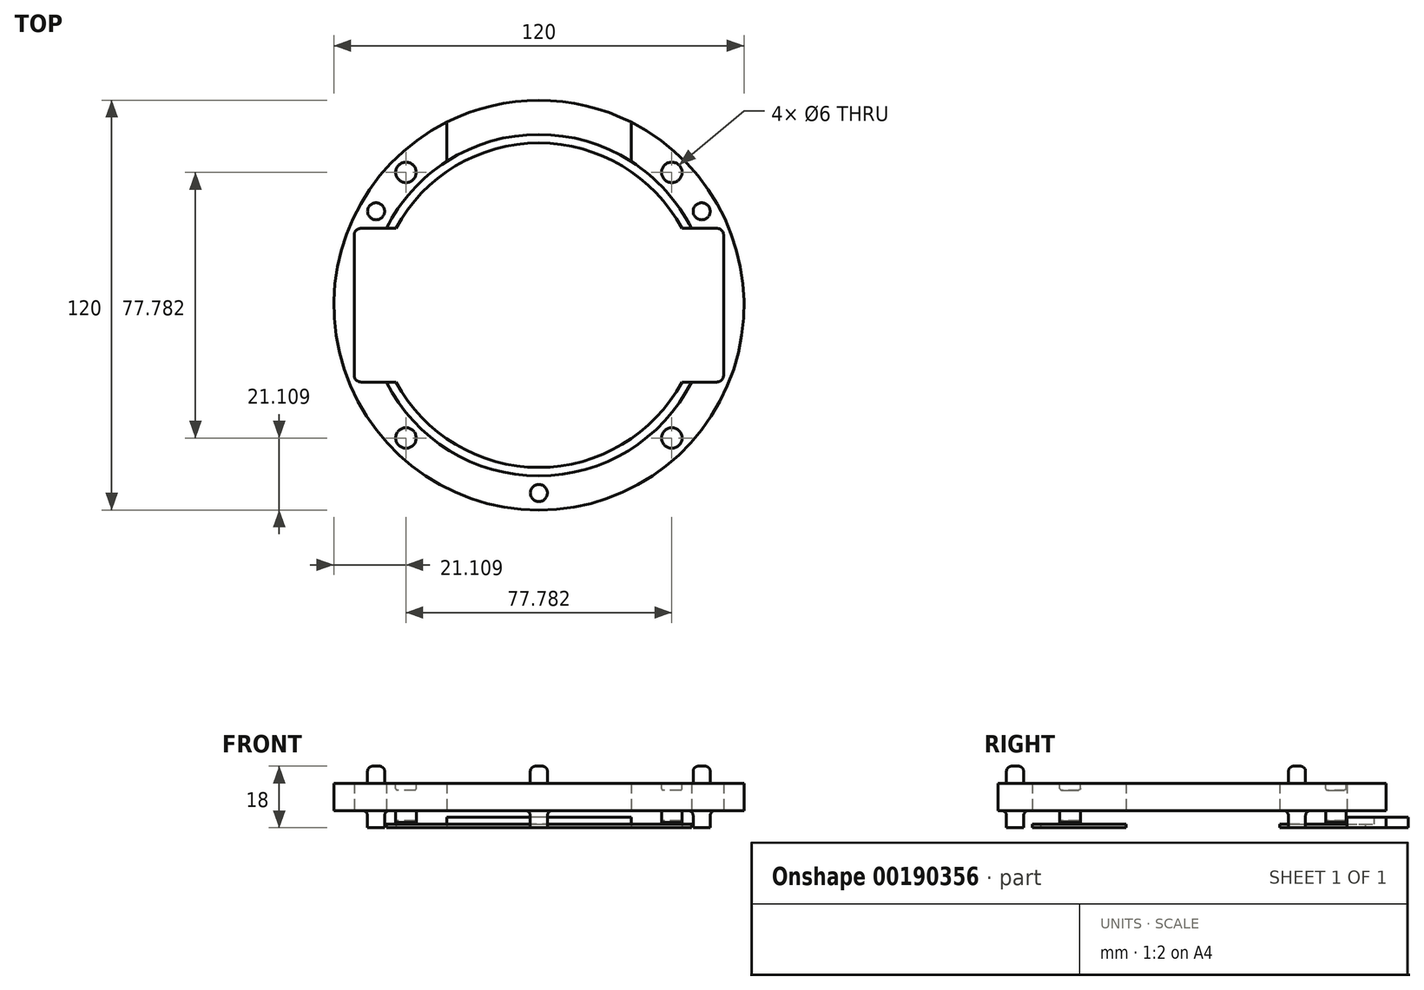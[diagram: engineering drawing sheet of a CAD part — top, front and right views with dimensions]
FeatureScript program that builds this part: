
annotation { "Feature Type Name" : "Feature", "Feature Type Description" : "" }
export const myFeature = defineFeature(function(context is Context, id is Id, definition is map)
    precondition{}
    {
        {
            var Q0;
            Q0=qCreatedBy(makeId("Top.planeOp"),FACE);
            var sketch = newSketch(context, id + "F0", { "sketchPlane" : qUnion([Q0])});
            skCircle(sketch, "E0", {"center": v(0, 0) * mm, "radius": 60 * mm});
            skLineSegment(sketch, "E1", {"start": v(0, 50) * mm, "end": v(0, 50) * mm});
            skArc(sketch, "E2", {"start": v(-44.65, -22.5) * mm, "mid": v(0, -50) * mm, "end": v(44.65, -22.5) * mm});
            skArc(sketch, "E3", {"start": v(-41.83, -22.5) * mm, "mid": v(0, -47.5) * mm, "end": v(41.83, -22.5) * mm});
            skPoint(sketch, "E4.orphan", {"position": v(55.62, -22.5) * mm});
            skLineSegment(sketch, "E5", {"start": v(-44.65, 22.5) * mm, "end": v(-41.83, 22.5) * mm});
            skLineSegment(sketch, "E6", {"start": v(44.65, 22.5) * mm, "end": v(41.83, 22.5) * mm});
            skLineSegment(sketch, "E7.MirrorCS", {"start": v(-44.65, -22.5) * mm, "end": v(-41.83, -22.5) * mm});
            skLineSegment(sketch, "E8.MirrorCS", {"start": v(44.65, -22.5) * mm, "end": v(41.83, -22.5) * mm});
            skArc(sketch, "E9.trimOffspring", {"start": v(41.83, 22.5) * mm, "mid": v(0, 47.5) * mm, "end": v(-41.83, 22.5) * mm});
            skArc(sketch, "E10.trimOffspring", {"start": v(44.65, 22.5) * mm, "mid": v(0, 50) * mm, "end": v(-44.65, 22.5) * mm});
            skLineSegment(sketch, "E11", {"start": v(-27, 53.58) * mm, "end": v(-27, 42.08) * mm});
            skLineSegment(sketch, "E12", {"start": v(27, 53.58) * mm, "end": v(27, 42.08) * mm});
            skLineSegment(sketch, "E13", {"start": v(-27, 53.58) * mm, "end": v(27, 53.58) * mm, "construction": true});
            skLineSegment(sketch, "E14", {"start": v(-44.65, 22.5) * mm, "end": v(-54.05, 22.5) * mm});
            skLineSegment(sketch, "E15", {"start": v(-54.05, 22.5) * mm, "end": v(-54.05, -22.5) * mm});
            skLineSegment(sketch, "E16", {"start": v(-54.05, -22.5) * mm, "end": v(-44.65, -22.5) * mm});
            skLineSegment(sketch, "E17", {"start": v(0, 60) * mm, "end": v(0, -60) * mm, "construction": true});
            skPoint(sketch, "E17.startSnap0", {"position": v(0, 53.58) * mm});
            skPoint(sketch, "E17.endSnap0", {"position": v(0, 47.5) * mm});
            skLineSegment(sketch, "E18.MirrorCS", {"start": v(54.05, 22.5) * mm, "end": v(54.05, -22.5) * mm});
            skLineSegment(sketch, "E19.MirrorCS", {"start": v(44.65, 22.5) * mm, "end": v(54.05, 22.5) * mm});
            skLineSegment(sketch, "E20.MirrorCS", {"start": v(54.05, -22.5) * mm, "end": v(44.65, -22.5) * mm});
            skSolve(sketch);
        }
        {
            var Q0;
            Q0=makeQuery(id+"F0.imprint","IMPRINT",FACE,{"disambiguationData":[TD([[makeQuery(id+"F0.imprint","IMPRINT",EDGE,{"derivedFrom":sQuery(id+"F0.wireOp",EDGE,"E2")}),-1.0]])]});
            extrude(context, id + "F1", {"entities" : qUnion([Q0]), "depth" : 13 * mm});
        }
        {
            var Q0;
            Q0=makeQuery(id+"F1.opExtrude","CAP_FACE",FACE,{"disambiguationData":[OSD([sQuery(id+"F0.wireOp",EDGE,"E0"),sQuery(id+"F0.wireOp",EDGE,"E1")])],"isStart":false});
            var sketch = newSketch(context, id + "F2", { "sketchPlane" : qUnion([Q0])});
            skPoint(sketch, "E21.middle", {"position": v(0, 0) * mm});
            skCircle(sketch, "E22", {"center": v(-38.9, 38.9) * mm, "radius": 3 * mm});
            skCircle(sketch, "E23", {"center": v(-38.9, -38.9) * mm, "radius": 3 * mm});
            skCircle(sketch, "E24", {"center": v(38.9, -38.9) * mm, "radius": 3 * mm});
            skCircle(sketch, "E25", {"center": v(38.9, 38.9) * mm, "radius": 3 * mm});
            skCircle(sketch, "E26", {"center": v(0, -55) * mm, "radius": 2.5 * mm});
            skCircle(sketch, "E27.1.0", {"center": v(47.63, 27.5) * mm, "radius": 2.5 * mm});
            skCircle(sketch, "E27.2.0", {"center": v(-47.63, 27.5) * mm, "radius": 2.5 * mm});
            skSolve(sketch);
        }
        {
            var Q0;
            Q0=makeQuery(id+"F2.imprint","IMPRINT",FACE,{"disambiguationData":[TD([[makeQuery(id+"F2.imprint","IMPRINT",EDGE,{"derivedFrom":sQuery(id+"F2.wireOp",EDGE,"E22")}),1.0]])]});
            var Q1;
            Q1=makeQuery(id+"F2.imprint","IMPRINT",FACE,{"disambiguationData":[TD([[makeQuery(id+"F2.imprint","IMPRINT",EDGE,{"derivedFrom":sQuery(id+"F2.wireOp",EDGE,"E25")}),1.0]])]});
            var Q2;
            Q2=makeQuery(id+"F2.imprint","IMPRINT",FACE,{"disambiguationData":[TD([[makeQuery(id+"F2.imprint","IMPRINT",EDGE,{"derivedFrom":sQuery(id+"F2.wireOp",EDGE,"E24")}),1.0]])]});
            var Q3;
            Q3=makeQuery(id+"F2.imprint","IMPRINT",FACE,{"disambiguationData":[TD([[makeQuery(id+"F2.imprint","IMPRINT",EDGE,{"derivedFrom":sQuery(id+"F2.wireOp",EDGE,"E23")}),1.0]])]});
            extrude(context, id + "F3", {"entities" : qUnion([Q0, Q1, Q2, Q3]), "operationType" : NewBodyOperationType.REMOVE, "oppositeDirection" : true, "depth" : 2 * mm});
        }
        {
            var Q0;
            Q0=makeQuery(id+"F2.imprint","IMPRINT",FACE,{"disambiguationData":[TD([[makeQuery(id+"F2.imprint","IMPRINT",EDGE,{"derivedFrom":sQuery(id+"F2.wireOp",EDGE,"E26")}),1.0]])]});
            var Q1;
            Q1=makeQuery(id+"F2.imprint","IMPRINT",FACE,{"disambiguationData":[TD([[makeQuery(id+"F2.imprint","IMPRINT",EDGE,{"derivedFrom":sQuery(id+"F2.wireOp",EDGE,"E27.1.0")}),1.0]])]});
            var Q2;
            Q2=makeQuery(id+"F2.imprint","IMPRINT",FACE,{"disambiguationData":[TD([[makeQuery(id+"F2.imprint","IMPRINT",EDGE,{"derivedFrom":sQuery(id+"F2.wireOp",EDGE,"E27.2.0")}),1.0]])]});
            var Q3;
            Q3=sQuery(id+"F2.wireOp",EDGE,"VWXdR3C8-mcWa-IJBR-1boV-t68bjsxYqndP");
            var Q4;
            Q4=sQuery(id+"F2.wireOp",EDGE,"uHltdg73-JYHf-iSAY-R7Fn-2nbyHwWvfhgZ");
            var Q5;
            Q5=sQuery(id+"F2.wireOp",EDGE,"R24LEf0a-MQ1t-eLEK-fKfR-x5qMptQUL0lt");
            extrude(context, id + "F4", {"entities" : qUnion([Q0, Q1, Q2]), "operationType" : NewBodyOperationType.ADD, "surfaceEntities" : qUnion([Q3, Q4, Q5]), "depth" : 5 * mm});
        }
        {
            var Q0;
            Q0=makeQuery(id+"F3.boolean.opBoolean","COPY",EDGE,{"derivedFrom":makeQuery(id+"F3.opExtrude","CAP_EDGE",EDGE,{"disambiguationData":[OSD([sQuery(id+"F2.wireOp",EDGE,"E24")])],"isStart":false})});
            var Q1;
            Q1=makeQuery(id+"F3.boolean.opBoolean","COPY",EDGE,{"derivedFrom":makeQuery(id+"F3.opExtrude","CAP_EDGE",EDGE,{"disambiguationData":[OSD([sQuery(id+"F2.wireOp",EDGE,"E23")])],"isStart":false})});
            var Q2;
            Q2=makeQuery(id+"F3.boolean.opBoolean","COPY",EDGE,{"derivedFrom":makeQuery(id+"F3.opExtrude","CAP_EDGE",EDGE,{"disambiguationData":[OSD([sQuery(id+"F2.wireOp",EDGE,"E22")])],"isStart":false})});
            var Q3;
            Q3=makeQuery(id+"F3.boolean.opBoolean","COPY",EDGE,{"derivedFrom":makeQuery(id+"F3.opExtrude","CAP_EDGE",EDGE,{"disambiguationData":[OSD([sQuery(id+"F2.wireOp",EDGE,"E25")])],"isStart":false})});
            fillet(context, id + "F5", {"entities" : qUnion([Q0, Q1, Q2, Q3]), "radius" : 0.5 * mm, "tangentPropagation" : true, "allowEdgeOverflow" : false});
        }
        {
            var Q0;
            Q0=makeQuery(id+"F0.imprint","IMPRINT",FACE,{"disambiguationData":[TD([[makeQuery(id+"F0.imprint","IMPRINT",EDGE,{"derivedFrom":sQuery(id+"F0.wireOp",EDGE,"E0")}),1.0]])]});
            var sketch = newSketch(context, id + "F6", { "sketchPlane" : qUnion([Q0])});
            skCircle(sketch, "E28.0", {"center": v(-38.9, 38.9) * mm, "radius": 3 * mm});
            skCircle(sketch, "E28.1", {"center": v(-38.9, -38.9) * mm, "radius": 3 * mm});
            skCircle(sketch, "E28.2", {"center": v(38.9, -38.9) * mm, "radius": 3 * mm});
            skCircle(sketch, "E28.3", {"center": v(38.9, 38.9) * mm, "radius": 3 * mm});
            skSolve(sketch);
        }
        {
            var Q0;
            Q0=makeQuery(id+"F6.imprint","IMPRINT",FACE,{"disambiguationData":[TD([[makeQuery(id+"F6.imprint","IMPRINT",EDGE,{"derivedFrom":sQuery(id+"F6.wireOp",EDGE,"E28.1")}),1.0]])]});
            var sketch = newSketch(context, id + "F7", { "sketchPlane" : qUnion([Q0])});
            skSolve(sketch);
        }
        {
            var Q0;
            Q0=makeQuery(id+"F7.imprint","IMPRINT",FACE,{"disambiguationData":[TD([[makeQuery(id+"F7.imprint","IMPRINT",EDGE,{"derivedFrom":makeQuery(id+"F6.imprint","IMPRINT",EDGE,{"derivedFrom":sQuery(id+"F6.wireOp",EDGE,"E28.1")})}),1.0]])]});
            var Q1;
            Q1=makeQuery(id+"F6.imprint","IMPRINT",FACE,{"disambiguationData":[TD([[makeQuery(id+"F6.imprint","IMPRINT",EDGE,{"derivedFrom":sQuery(id+"F6.wireOp",EDGE,"E28.2")}),1.0]])]});
            var Q2;
            Q2=makeQuery(id+"F6.imprint","IMPRINT",FACE,{"disambiguationData":[TD([[makeQuery(id+"F6.imprint","IMPRINT",EDGE,{"derivedFrom":sQuery(id+"F6.wireOp",EDGE,"E28.3")}),1.0]])]});
            var Q3;
            Q3=makeQuery(id+"F6.imprint","IMPRINT",FACE,{"disambiguationData":[TD([[makeQuery(id+"F6.imprint","IMPRINT",EDGE,{"derivedFrom":sQuery(id+"F6.wireOp",EDGE,"E28.0")}),1.0]])]});
            var Q4;
            Q4=sQuery(id+"F6.wireOp",EDGE,"E28.2");
            var Q5;
            Q5=sQuery(id+"F6.wireOp",EDGE,"E28.3");
            var Q6;
            Q6=sQuery(id+"F6.wireOp",EDGE,"E28.0");
            var Q7;
            Q7=sQuery(id+"F6.wireOp",EDGE,"E28.1");
            extrude(context, id + "F8", {"entities" : qUnion([Q0, Q1, Q2, Q3]), "operationType" : NewBodyOperationType.REMOVE, "surfaceEntities" : qUnion([Q4, Q5, Q6, Q7]), "depth" : 2 * mm});
        }
        {
            var Q0;
            Q0=makeQuery(id+"F8.boolean.opBoolean","COPY",EDGE,{"derivedFrom":makeQuery(id+"F8.opExtrude","CAP_EDGE",EDGE,{"disambiguationData":[OSD([sQuery(id+"F6.wireOp",EDGE,"E28.3")])],"isStart":false})});
            var Q1;
            Q1=makeQuery(id+"F8.boolean.opBoolean","COPY",EDGE,{"derivedFrom":makeQuery(id+"F8.opExtrude","CAP_EDGE",EDGE,{"disambiguationData":[OSD([sQuery(id+"F6.wireOp",EDGE,"E28.2")])],"isStart":false})});
            var Q2;
            Q2=makeQuery(id+"F8.boolean.opBoolean","COPY",EDGE,{"derivedFrom":makeQuery(id+"F8.opExtrude","CAP_EDGE",EDGE,{"disambiguationData":[OSD([sQuery(id+"F6.wireOp",EDGE,"E28.1")])],"isStart":false})});
            var Q3;
            Q3=makeQuery(id+"F8.boolean.opBoolean","COPY",EDGE,{"derivedFrom":makeQuery(id+"F8.opExtrude","CAP_EDGE",EDGE,{"disambiguationData":[OSD([sQuery(id+"F6.wireOp",EDGE,"E28.0")])],"isStart":false})});
            fillet(context, id + "F9", {"entities" : qUnion([Q0, Q1, Q2, Q3]), "radius" : 0.5 * mm, "tangentPropagation" : true, "allowEdgeOverflow" : false});
        }
        {
            var Q0;
            Q0=makeQuery(id+"F1.opExtrude","CAP_FACE",FACE,{"disambiguationData":[OSD([sQuery(id+"F0.wireOp",EDGE,"E0"),sQuery(id+"F0.wireOp",EDGE,"E1")])],"isStart":true});
            var sketch = newSketch(context, id + "F10", { "sketchPlane" : qUnion([Q0])});
            skCircle(sketch, "E29.0", {"center": v(0, 55) * mm, "radius": 2.5 * mm});
            skCircle(sketch, "E29.1", {"center": v(47.63, -27.5) * mm, "radius": 2.5 * mm});
            skCircle(sketch, "E29.2", {"center": v(-47.63, -27.5) * mm, "radius": 2.5 * mm});
            skSolve(sketch);
        }
        {
            var Q0;
            Q0=makeQuery(id+"F10.imprint","IMPRINT",FACE,{"disambiguationData":[TD([[makeQuery(id+"F10.imprint","IMPRINT",EDGE,{"derivedFrom":sQuery(id+"F10.wireOp",EDGE,"E29.2")}),-1.0]])]});
            var Q1;
            Q1=makeQuery(id+"F10.imprint","IMPRINT",FACE,{"disambiguationData":[TD([[makeQuery(id+"F10.imprint","IMPRINT",EDGE,{"derivedFrom":sQuery(id+"F10.wireOp",EDGE,"E29.0")}),-1.0]])]});
            var Q2;
            Q2=makeQuery(id+"F10.imprint","IMPRINT",FACE,{"disambiguationData":[TD([[makeQuery(id+"F10.imprint","IMPRINT",EDGE,{"derivedFrom":sQuery(id+"F10.wireOp",EDGE,"E29.1")}),-1.0]])]});
            extrude(context, id + "F11", {"entities" : qUnion([Q0, Q1, Q2]), "operationType" : NewBodyOperationType.REMOVE, "oppositeDirection" : true, "depth" : 5 * mm});
        }
        {
            var Q0;
            Q0=makeQuery(id+"F4.opExtrude","CAP_EDGE",EDGE,{"disambiguationData":[OSD([sQuery(id+"F2.wireOp",EDGE,"E26")])],"isStart":false});
            var Q1;
            Q1=makeQuery(id+"F4.opExtrude","CAP_EDGE",EDGE,{"disambiguationData":[OSD([sQuery(id+"F2.wireOp",EDGE,"E27.2.0")])],"isStart":false});
            var Q2;
            Q2=makeQuery(id+"F4.opExtrude","CAP_EDGE",EDGE,{"disambiguationData":[OSD([sQuery(id+"F2.wireOp",EDGE,"E27.1.0")])],"isStart":false});
            var Q3;
            Q3=makeQuery(id+"F11.boolean.opBoolean","COPY",EDGE,{"derivedFrom":makeQuery(id+"F11.opExtrude","CAP_EDGE",EDGE,{"disambiguationData":[OSD([sQuery(id+"F10.wireOp",EDGE,"E29.0")])],"isStart":false})});
            var Q4;
            Q4=makeQuery(id+"F11.boolean.opBoolean","COPY",EDGE,{"derivedFrom":makeQuery(id+"F11.opExtrude","CAP_EDGE",EDGE,{"disambiguationData":[OSD([sQuery(id+"F10.wireOp",EDGE,"E29.1")])],"isStart":false})});
            var Q5;
            Q5=makeQuery(id+"F11.boolean.opBoolean","COPY",EDGE,{"derivedFrom":makeQuery(id+"F11.opExtrude","CAP_EDGE",EDGE,{"disambiguationData":[OSD([sQuery(id+"F10.wireOp",EDGE,"E29.2")])],"isStart":false})});
            fillet(context, id + "F12", {"entities" : qUnion([Q0, Q1, Q2, Q3, Q4, Q5]), "radius" : 1.5 * mm, "tangentPropagation" : true, "allowEdgeOverflow" : false});
        }
        {
            var Q0;
            Q0=makeQuery(id+"F1.opExtrude","SWEPT_BODY",BODY,{"disambiguationData":[OSD([sQuery(id+"F0.wireOp",EDGE,"E0"),sQuery(id+"F0.wireOp",EDGE,"E1"),sQuery(id+"F0.wireOp",EDGE,"Z948ch8O-qMHw-9Xcc-9FHW-eBQYffAlLzsf"),sQuery(id+"F0.wireOp",EDGE,"A77KNi0v-6heQ-Jye2-6KwH-JstxTwlQuu4X.top"),sQuery(id+"F0.wireOp",EDGE,"A77KNi0v-6heQ-Jye2-6KwH-JstxTwlQuu4X.left"),sQuery(id+"F0.wireOp",EDGE,"A77KNi0v-6heQ-Jye2-6KwH-JstxTwlQuu4X.right"),sQuery(id+"F0.wireOp",EDGE,"e3c13985-3201-4729-a912-cdfdbae41750.trimOffspring"),sQuery(id+"F0.wireOp",EDGE,"hgyFUOab-B19C-UYkE-toPB-BuUCfqlj2oRy.bottom")])]});
            transform(context, id + "F13", {"entities" : qUnion([Q0]), "transformType" : TransformType.TRANSLATION_3D, "dx" : 0 * mm, "dy" : 0 * mm, "dz" : 0 * mm, "makeCopy" : true});
        }
        {
            var Q0;
            Q0=makeQuery(id+"F13.opPattern","COPY",BODY,{"derivedFrom":makeQuery(id+"F1.opExtrude","SWEPT_BODY",BODY,{"disambiguationData":[OSD([sQuery(id+"F0.wireOp",EDGE,"E0"),sQuery(id+"F0.wireOp",EDGE,"E1"),sQuery(id+"F0.wireOp",EDGE,"Z948ch8O-qMHw-9Xcc-9FHW-eBQYffAlLzsf"),sQuery(id+"F0.wireOp",EDGE,"A77KNi0v-6heQ-Jye2-6KwH-JstxTwlQuu4X.top"),sQuery(id+"F0.wireOp",EDGE,"A77KNi0v-6heQ-Jye2-6KwH-JstxTwlQuu4X.left"),sQuery(id+"F0.wireOp",EDGE,"A77KNi0v-6heQ-Jye2-6KwH-JstxTwlQuu4X.right"),sQuery(id+"F0.wireOp",EDGE,"e3c13985-3201-4729-a912-cdfdbae41750.trimOffspring"),sQuery(id+"F0.wireOp",EDGE,"hgyFUOab-B19C-UYkE-toPB-BuUCfqlj2oRy.bottom")])]}),"instanceName":"1"});
            deleteBodies(context, id + "F14", {"entities" : qUnion([Q0])});
        }
        {
            var Q0;
            Q0=makeQuery(id+"F0.imprint","IMPRINT",FACE,{"disambiguationData":[TD([[makeQuery(id+"F0.imprint","IMPRINT",EDGE,{"derivedFrom":sQuery(id+"F0.wireOp",EDGE,"E2")}),1.0]])]});
            var sketch = newSketch(context, id + "F15", { "sketchPlane" : qUnion([Q0])});
            skSolve(sketch);
        }
        {
            var Q0;
            Q0=qSketchRegion(id+"F15",true);
            var Q1;
            Q1=makeQuery(id+"F0.imprint","IMPRINT",FACE,{"disambiguationData":[TD([[makeQuery(id+"F0.imprint","IMPRINT",EDGE,{"derivedFrom":sQuery(id+"F0.wireOp",EDGE,"E2")}),1.0]])]});
            var Q2;
            Q2=makeQuery(id+"F0.imprint","IMPRINT",FACE,{"disambiguationData":[TD([[makeQuery(id+"F0.imprint","IMPRINT",EDGE,{"derivedFrom":sQuery(id+"F0.wireOp",EDGE,"E5")}),1.0]])]});
            extrude(context, id + "F16", {"entities" : qUnion([Q0, Q1, Q2]), "operationType" : NewBodyOperationType.ADD, "depth" : 1 * mm});
        }
        {
            var Q0;
            {var subQ0=sQuery(id+"F0.wireOp",EDGE,"E11");Q0=makeQuery(id+"F0.imprint","IMPRINT",FACE,{"disambiguationData":[TD([[makeQuery(id+"F0.imprint","IMPRINT",EDGE,{"derivedFrom":subQ0}),1.0]])]});}
            extrude(context, id + "F17", {"entities" : qUnion([Q0]), "operationType" : NewBodyOperationType.ADD, "depth" : 3 * mm});
        }
        {
            var Q0;
            Q0=makeQuery(id+"F1.opExtrude","SWEPT_EDGE",EDGE,{"disambiguationData":[OSD([sQuery(id+"F0.wireOp",EDGE,"E14"),sQuery(id+"F0.wireOp",EDGE,"E15")])]});
            var Q1;
            Q1=makeQuery(id+"F1.opExtrude","SWEPT_EDGE",EDGE,{"disambiguationData":[OSD([sQuery(id+"F0.wireOp",EDGE,"E18.MirrorCS"),sQuery(id+"F0.wireOp",EDGE,"E19.MirrorCS")])]});
            var Q2;
            Q2=makeQuery(id+"F1.opExtrude","SWEPT_EDGE",EDGE,{"disambiguationData":[OSD([sQuery(id+"F0.wireOp",EDGE,"E18.MirrorCS"),sQuery(id+"F0.wireOp",EDGE,"E20.MirrorCS")])]});
            var Q3;
            Q3=makeQuery(id+"F1.opExtrude","SWEPT_EDGE",EDGE,{"disambiguationData":[OSD([sQuery(id+"F0.wireOp",EDGE,"E15"),sQuery(id+"F0.wireOp",EDGE,"E16")])]});
            fillet(context, id + "F18", {"entities" : qUnion([Q0, Q1, Q2, Q3]), "radius" : 2 * mm, "tangentPropagation" : true, "allowEdgeOverflow" : false});
        }
    });
